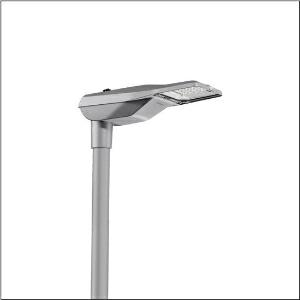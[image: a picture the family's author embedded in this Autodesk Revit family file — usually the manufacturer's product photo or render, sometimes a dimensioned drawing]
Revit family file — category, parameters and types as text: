
# Revit family: streetlight_sl_21_iq_micro___p0_8ab_5xe1r31v08db_6cb1
name_source: partatom
category: Lighting Fixtures
units: mm (PartAtom-declared; Revit-internal decimal feet)

## family parameters
Cut with Voids When Loaded = No
Host = Face
Light Source = No
Part Type = Normal
Room Calculation Point = No
Round Connector Dimension = Use Diameter
Shared = No

## types (1)
- --- (1 x LED, 4550 lm, 39.1 W, 3000K)
    Apparent Load = 39 VA
    CIE Flux Codes = 36 71 98 100 100
    Color Rendering = 70
    Color Temperature = 3000K
    Default Elevation = 1800 mm
    Description = Streetlight SL 21 iQ micro, mast luminaire, primary light control with lens, of PMMA, primary optical cover: cover, of toughened safety glass, transparent, light distribution: P0.8aB, light emission: direct distribution, primary light characteristic: asymmetric, installation type: post-top, side-entry, LED, High Power LED, rated luminous flux: 4.550lm, luminous efficacy: 116lm/W, light colour: 730, colour temperature: 3000K, control gear: iQ-Street Remote, D4i with power reduction, control: pre-setting: logarithmic dimming characteristic, Street-Remote, Auto-Match, Temp-Guard, Lumen-Switch, Night-Set, Smart-Wire, Light-Fading, Desk-Remote (wireless, voltage-free reading and setting of iQ features in the workshop via application-optimized NFC function/RFID function), optimised constant luminous flux control (CLO 2.0), mains connection: 220..240V, AC, 50/60Hz, start of lifetime: 39W, end of service life: 41W, reduction: 17W, luminaire housing, of diecast aluminium, powder-coated, Siteco® metallic grey (DB 702S), corrosivity category C5 high according to DIN EN ISO 12944, please order mast flange separately, inclination adjustable: 0°, 5°, 10°, 15°, sealing non-destructively replaceable, multi-level sealing system, length: 528mm, width: 235mm, height: 110mm, mast flange for spigot size: 42mm (side-entry): 5XC10008XM4, 60/48mm (side-entry/post-top): 5XC10108XM2, 76/60mm (side-entry/post-top): 5XC10108XM1, mounting height: 4..8m, Smart Interface above, protection rating (complete): IP66, insulation class (complete): insulation class II (safety insulation), certification: CE, ENEC, ENEC+, VDE, impact resistance: IK10, permissible operating ambient temperature for outdoor applications: -40..+50°C, standard-compliant lighting for roads and squares, packaging unit: 1 piece

Light Distribution: P0.8aB
    Height = 110 mm
    Lamp = 1 x LED
    Lamp Light Flux = 4550 lm
    Lamp Power = 39.1 W
    Lamp count = 1
    Length = 528 mm
    Luminous efficacy = 116 lm/W
    Manufacturer = Siteco
    ModVariant = No
    Model = 5XE1R31V08DB
    Number of Poles = 1
    OnlyDefault = Yes
    Power Factor = 1
    Product Name = Streetlight SL 21 iQ micro | P0.8aB
    Product group = mast luminaire | pylon top
    ProductGroupID = 6100
    Protection Class = Protection class II
    Protection Degree = IP 66
    RLX_Detail_Level = 1
    RLX_Emergency_Light_Flux = 0 lm
    RLX_Emergency_Type = 0
    RLX_Emergency_Type_DB = No
    RlxData = <blob elided: 98665 chars, md5=0f4f71ab>
    Socket = socket
    Standby Power = 0 W
    System Light Flux = 4550 lm
    System Power = 39 W
    Type Comments = factory setting: luminous flux: 100 % | dim-lin: 254 | 765 mA
    Type Image = l_1277292.jpg
    URL = http://relux.com
    VarID = @adj_086039
    Voltage = 0 V
    Weight = 0.00 kg
    Width = 235 mm

## geometry (parser evidence)
native form markers: Blend x4, Sweep x11
no freeform markers — native parametric forms only
